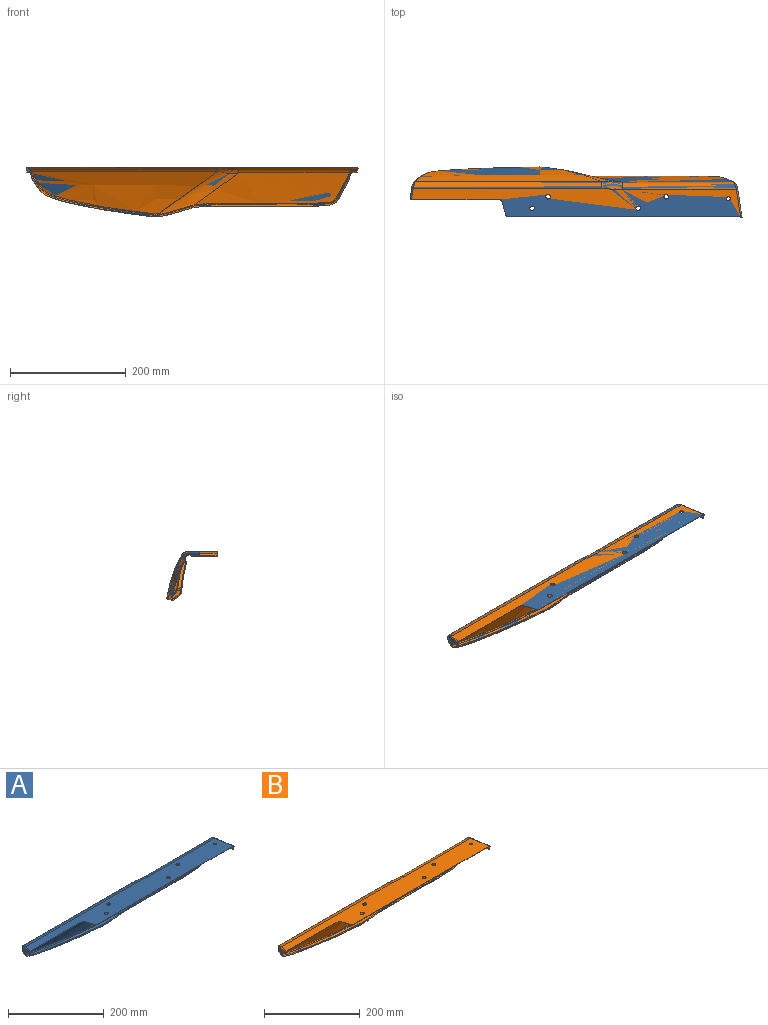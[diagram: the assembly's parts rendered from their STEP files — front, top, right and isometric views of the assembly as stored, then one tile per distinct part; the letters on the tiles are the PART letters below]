
ASSEMBLY  parts=2 mates=1
PART A: 90 faces, bbox 580.2x94.9x176.3 mm
  f0: bspline ~57.87x17.81mm, area 111.5mm2, adj f1,f8,f9,f10
  f1: bspline ~2.59x2.25mm, area 3.8mm2, adj f0,f3,f8,f11
  f2: bspline ~59.87x17.64mm, area 166.5mm2, adj f4,f8,f15,f16,f17
  f3: bspline ~5.04x2.61mm, area 12.2mm2, adj f1,f11,f20,f21
  f4: bspline ~3.74x2.35mm, area 7.8mm2, adj f2,f5,f15,f21
  f5: torus R=36.8mm, axis (0,0.99,0.14), area 2mm2, adj f4,f7,f14,f21
  f6: bspline ~217.18x70.26mm, area 164.9mm2, adj f7,f14,f23,f24
  f7: bspline ~218.59x72.83mm, area 627.5mm2, adj f5,f6,f14,f24,f42
  f8: bspline ~59.27x24.67mm, area 409.1mm2, adj f0,f1,f2,f21,f27
  f9: bspline ~146.09x75.43mm, area 2805mm2, adj f0,f10,f11,f12,f13,f28
  f10: bspline ~2.23x2.04mm, area 2.4mm2, adj f0,f9,f27,f28
  f11: extruded ~321.58x73.69mm, area 17042.7mm2, adj f1,f3,f9,f20,f31
  f12: bspline ~36.97x16.66mm, area 543.4mm2, adj f9,f31,f32,f51
  f13: cylinder r=332.11mm len=267.86mm, axis (-1,0,0), area 5366mm2, adj f9,f29,f32
  f14: cylinder r=36.8mm len=1.03mm, axis (0,0.99,0.14), area 0.7mm2, adj f5,f6,f7,f15,f23,f33
  f15: bspline ~3.73x1.01mm, area 2.1mm2, adj f2,f4,f14,f17,f34,f36
  f16: bspline ~2.22x1.98mm, area 1.2mm2, adj f2,f18,f27,f37
  f17: bspline ~59.5x16.5mm, area 43.8mm2, adj f2,f15,f36,f37
  f18: bspline ~2.25x2mm, area 1.2mm2, adj f16,f27,f38,f39,f40
  f19: bspline ~12.63x8.98mm, area 46.4mm2, adj f20,f31,f41,f42
  f20: bspline ~218.45x77.65mm, area 737.8mm2, adj f3,f11,f19,f42
  f21: cylinder r=35.1mm len=5.62mm, axis (0,-0.99,-0.14), area 22.5mm2, adj f3,f4,f5,f8,f42
  f22: plane 14.14x2.5mm, normal (-0.91,0.14,-0.39), area 9.1mm2, adj f26,f43,f44,f45
  f23: bspline ~218.25x71.79mm, area 370.7mm2, adj f6,f14,f24,f33,f46,f53
  f24: cylinder r=8.22mm len=7.66mm, axis (-0.91,0.14,-0.38), area 5.9mm2, adj f6,f7,f23,f25,f42,f46
  f25: extruded ~7.12x4.52mm, area 6.4mm2, adj f24,f26,f42,f46
  f26: cylinder r=8.22mm len=6.56mm, axis (-0.91,0.14,-0.38), area 5.3mm2, adj f22,f25,f42,f43,f45,f46
  f27: extruded ~5.77x1.11mm, area 5.4mm2, adj f8,f10,f16,f18,f49
  f28: bspline ~6.14x3.79mm, area 13.9mm2, adj f9,f10,f29,f49
  f29: bspline ~273.24x59.78mm, area 873.8mm2, adj f13,f28,f30,f49
  f30: bspline ~13.76x11.39mm, area 56.4mm2, adj f29,f32,f49,f50
  f31: cylinder r=12.8mm len=325.37mm, axis (1,0,0), area 4378.8mm2, adj f11,f12,f19,f51
  f32: cylinder r=12.8mm len=196.45mm, axis (1,0,0), area 3218.4mm2, adj f12,f13,f30,f51
  f33: torus R=36.8mm, axis (0,0.99,0.14), area 1.4mm2, adj f14,f23,f34,f53
  f34: bspline ~3.67x1.43mm, area 4.6mm2, adj f15,f33,f36,f53
  f35: bspline ~219.21x78.81mm, area 1012.1mm2, adj f46,f52,f54,f55
  f36: bspline ~59.48x16.86mm, area 97.9mm2, adj f15,f17,f34,f56,f76
  f37: plane 0.72x0.44mm, normal (0.25,0.14,-0.96), area 0.3mm2, adj f16,f17,f38,f56,f57
  f38: plane 0.7x0.45mm, normal (0.24,0.14,-0.96), area 0.3mm2, adj f18,f37,f40,f57
  f39: bspline ~278.01x57.08mm, area 795.8mm2, adj f18,f40,f49,f59
  f40: bspline ~276.67x54.6mm, area 208.9mm2, adj f18,f38,f39,f57,f59,f60
  f41: cylinder r=1.9mm len=19.81mm, axis (-0.15,-0.99,0), area 72.8mm2, adj f19,f42,f51,f65
  f42: bspline ~226.03x87.31mm, area 1355.3mm2, adj f7,f19,f20,f21,f24,f25,f26,f41
  f43: bspline ~16.19x4.06mm, area 37.4mm2, adj f22,f26,f42,f44,f65
  f44: bspline ~1.29x1.29mm, area 0.4mm2, adj f22,f43,f45,f65
  f45: bspline ~16.16x3.26mm, area 23.4mm2, adj f22,f26,f44,f46,f65
  f46: bspline ~225.86x87.7mm, area 1360.2mm2, adj f23,f24,f25,f26,f35,f45,f52,f53
  f47: bspline ~42.53x6.81mm, area 29.2mm2, adj f48,f61,f62,f68
  f48: bspline ~44.16x8.36mm, area 113.2mm2, adj f47,f49,f62,f68
  f49: bspline ~291.39x79.44mm, area 1902.9mm2, adj f27,f28,f29,f30,f39,f48,f50,f58
  f50: bspline ~48.61x10.3mm, area 179.1mm2, adj f30,f49,f51,f68
  f51: plane 572.5x53.85mm, normal (0,0,-1), area 22246.1mm2, adj f12,f31,f32,f41,f50,f63,f64,f65
  f52: bspline ~13.57x10.12mm, area 65.9mm2, adj f35,f46,f66,f75
  f53: cylinder r=35.8mm len=5.62mm, axis (0,-0.99,-0.14), area 23.1mm2, adj f23,f33,f34,f46,f55,f76
  f54: extruded ~321.58x73.94mm, area 17098.9mm2, adj f35,f55,f75,f77,f88
  f55: bspline ~5.16x3.53mm, area 17mm2, adj f35,f53,f54,f77
  f56: bspline ~1.23x0.99mm, area 0.6mm2, adj f36,f37,f57,f78
  f57: revolved ~101.54x100.52mm, area 498.9mm2, adj f37,f38,f40,f56,f60,f78
  f58: extruded ~7.91x6.39mm, area 8mm2, adj f49,f59,f62,f79
  f59: cylinder r=8.52mm len=7.6mm, axis (0.91,0.14,-0.4), area 6.4mm2, adj f39,f40,f49,f58,f60,f79
  f60: bspline ~277.38x55.93mm, area 469.4mm2, adj f40,f57,f59,f79
  f61: bspline ~44.08x7.55mm, area 67.3mm2, adj f47,f62,f68,f79
  f62: cylinder r=8.52mm len=6.6mm, axis (0.91,0.14,-0.4), area 5.4mm2, adj f47,f48,f49,f58,f61,f79
  f63: plane 22.59x6.05mm, normal (-0.97,-0.26,0), area 16.4mm2, adj f51,f64,f69,f81
  f64: cylinder r=5mm len=4.83mm, axis (0,0,1), area 4.6mm2, adj f51,f63,f65,f81
  f65: plane 154.45x9.53mm, normal (0,-1,0), area 113.4mm2, adj f41,f42,f43,f44,f45,f46,f51,f64
  f66: cylinder r=2.6mm len=20.01mm, axis (-0.15,-0.99,0), area 99.9mm2, adj f46,f52,f65,f81
  f67: bspline ~48.89x11.39mm, area 245.4mm2, adj f68,f79,f80,f81
  f68: plane 403.75x9.65mm, normal (0,-1,0), area 288.1mm2, adj f47,f48,f49,f50,f51,f61,f67,f69
  f69: cylinder r=5mm len=4.83mm, axis (0,0,1), area 4.6mm2, adj f51,f63,f68,f81
  f70: cylinder r=4mm len=8mm, axis (0,0,-1), area 17.6mm2, adj f51,f81
  f71: cylinder r=3.5mm len=7mm, axis (0,0,1), area 15.4mm2, adj f51,f81
  f72: cylinder r=4mm len=8mm, axis (0,0,-1), area 17.6mm2, adj f51,f81
  f73: cylinder r=4mm len=8mm, axis (0,0,-1), area 17.6mm2, adj f51,f81
  f74: cylinder r=4mm len=8mm, axis (0,0,-1), area 17.6mm2, adj f51,f81
  f75: cylinder r=13.5mm len=325.37mm, axis (1,0,0), area 4618.3mm2, adj f52,f54,f81,f82
  f76: bspline ~59.17x24.64mm, area 409.9mm2, adj f36,f53,f77,f78,f83
  f77: bspline ~3.48x3.07mm, area 5.1mm2, adj f54,f55,f76,f83
  f78: extruded ~5.77x1.1mm, area 5.3mm2, adj f56,f57,f76,f79,f84
  f79: bspline ~290.6x78.78mm, area 1907.3mm2, adj f58,f59,f60,f61,f62,f67,f68,f78
  f80: bspline ~14.78x12.52mm, area 79.9mm2, adj f67,f79,f86,f87
  f81: plane 572.79x54.07mm, normal (0,0,1), area 22245.9mm2, adj f63,f64,f65,f66,f67,f68,f69,f70
  f82: bspline ~36.97x17.52mm, area 573mm2, adj f75,f81,f87,f88
  f83: bspline ~58.12x18.63mm, area 153mm2, adj f76,f77,f84,f88
  f84: bspline ~2.96x2.75mm, area 3.2mm2, adj f78,f83,f85,f88
  f85: bspline ~6.2x4.73mm, area 18.8mm2, adj f79,f84,f86,f88
  f86: bspline ~274.1x60.76mm, area 1198.9mm2, adj f79,f80,f85,f89
  f87: cylinder r=13.5mm len=196.45mm, axis (1,0,0), area 3394.4mm2, adj f80,f81,f82,f89
  f88: bspline ~146.12x75.95mm, area 2845mm2, adj f54,f82,f83,f84,f85,f89
  f89: cylinder r=332.81mm len=267.87mm, axis (-1,0,0), area 5377.9mm2, adj f86,f87,f88
PART B: 90 faces, bbox 586.4x101x101.5 mm
  f0: plane 578.95x60.2mm, normal (0,0,1), area 22245.8mm2, adj f1,f3,f4,f5,f6,f7,f8,f9
  f1: cylinder r=4mm len=8mm, axis (0,0,-1), area 20.1mm2, adj f0,f2
  f2: plane 578.79x60.05mm, normal (0,0,-1), area 22245.7mm2, adj f1,f3,f4,f5,f6,f7,f8,f9
  f3: cylinder r=4mm len=8mm, axis (0,0,-1), area 20.1mm2, adj f0,f2
  f4: cylinder r=3.5mm len=7mm, axis (0,0,1), area 17.6mm2, adj f0,f2
  f5: cylinder r=4mm len=8mm, axis (0,0,-1), area 20.1mm2, adj f0,f2
  f6: cylinder r=4mm len=8mm, axis (0,0,-1), area 20.1mm2, adj f0,f2
  f7: plane 22.59x6.05mm, normal (-0.97,-0.26,0), area 18.7mm2, adj f0,f2,f8,f23
  f8: cylinder r=5mm len=4.83mm, axis (0,0,1), area 5.2mm2, adj f0,f2,f7,f9
  f9: plane 403.74x9.73mm, normal (0,-1,0), area 329.2mm2, adj f0,f2,f8,f10,f36,f37,f39,f87
  f10: bspline ~48.89x11.43mm, area 245.4mm2, adj f0,f9,f11,f39
  f11: bspline ~14.78x12.52mm, area 79.9mm2, adj f10,f12,f39,f85
  f12: cylinder r=13.5mm len=196.45mm, axis (1,0,0), area 3394.4mm2, adj f0,f11,f13,f86
  f13: bspline ~36.97x17.52mm, area 573mm2, adj f0,f12,f14,f20
  f14: bspline ~146.12x75.95mm, area 2845.3mm2, adj f13,f15,f17,f83,f84,f86
  f15: bspline ~58.12x18.63mm, area 152.9mm2, adj f14,f16,f47,f83
  f16: bspline ~3.48x3.07mm, area 5.1mm2, adj f15,f17,f47,f82
  f17: extruded ~321.58x73.94mm, area 17116.6mm2, adj f14,f16,f18,f20,f82
  f18: bspline ~219.21x78.81mm, area 1030.6mm2, adj f17,f19,f53,f82
  f19: bspline ~13.57x10.12mm, area 65.9mm2, adj f18,f20,f21,f53
  f20: cylinder r=13.5mm len=325.37mm, axis (1,0,0), area 4618.3mm2, adj f0,f13,f17,f19
  f21: cylinder r=2.6mm len=20.01mm, axis (-0.15,-0.99,0), area 99.9mm2, adj f0,f19,f22,f53
  f22: plane 154.45x9.65mm, normal (0,-1,0), area 129.3mm2, adj f0,f2,f21,f23,f24,f53,f54,f55
  f23: cylinder r=5mm len=4.83mm, axis (0,0,1), area 5.2mm2, adj f0,f2,f7,f22
  f24: cylinder r=1.8mm len=19.78mm, axis (-0.15,-0.99,0), area 68.9mm2, adj f2,f22,f25,f57
  f25: bspline ~12.5x8.82mm, area 43.8mm2, adj f24,f26,f57,f58
  f26: cylinder r=12.7mm len=325.37mm, axis (1,0,0), area 4344.6mm2, adj f2,f25,f27,f59
  f27: bspline ~36.97x16.53mm, area 539.2mm2, adj f2,f26,f28,f34
  f28: bspline ~146.09x75.41mm, area 2797.6mm2, adj f27,f29,f30,f31,f33,f59
  f29: bspline ~57.84x17.69mm, area 105.5mm2, adj f28,f30,f60,f61
  f30: bspline ~2.13x1.94mm, area 2.2mm2, adj f28,f29,f31,f64
  f31: bspline ~6.13x3.66mm, area 13.2mm2, adj f28,f30,f32,f37
  f32: bspline ~273.14x59.64mm, area 826mm2, adj f31,f33,f35,f37
  f33: cylinder r=332.01mm len=267.86mm, axis (-1,0,0), area 11529.5mm2, adj f28,f32,f34
  f34: cylinder r=12.7mm len=196.45mm, axis (1,0,0), area 3193.3mm2, adj f2,f27,f33,f35
  f35: bspline ~13.62x11.23mm, area 53.1mm2, adj f32,f34,f36,f37
  f36: bspline ~48.58x10.17mm, area 169.7mm2, adj f2,f9,f35,f37
  f37: bspline ~291.32x79.38mm, area 1905.2mm2, adj f9,f31,f32,f35,f36,f38,f40,f41
  f38: extruded ~7.92x6.43mm, area 9.1mm2, adj f37,f39,f40,f41
  f39: bspline ~290.6x78.78mm, area 1907.3mm2, adj f9,f10,f11,f38,f40,f41,f42,f44
  f40: cylinder r=8.52mm len=7.72mm, axis (0.91,0.14,-0.4), area 7.4mm2, adj f37,f38,f39,f42,f66,f67
  f41: cylinder r=8.52mm len=6.71mm, axis (0.91,0.14,-0.4), area 6.2mm2, adj f37,f38,f39,f87,f88,f89
  f42: bspline ~277.37x55.92mm, area 468.1mm2, adj f39,f40,f43,f67
  f43: revolved ~1.23x0.87mm, area 0.8mm2, adj f42,f44,f45,f68
  f44: extruded ~5.77x1.1mm, area 5.3mm2, adj f39,f43,f45,f47,f83
  f45: bspline ~1.24x0.99mm, area 0.7mm2, adj f43,f44,f46,f69
  f46: bspline ~59.48x16.86mm, area 98mm2, adj f45,f47,f70,f79
  f47: bspline ~59.17x24.65mm, area 409.8mm2, adj f15,f16,f44,f46,f48
  f48: cylinder r=35.8mm len=5.62mm, axis (0,-0.99,-0.14), area 23.1mm2, adj f47,f49,f50,f53,f79,f82
  f49: torus R=36.8mm, axis (0,0.99,0.14), area 1.4mm2, adj f48,f50,f75,f79
  f50: bspline ~218.25x71.79mm, area 370.2mm2, adj f48,f49,f52,f53,f75,f77
  f51: cylinder r=8.22mm len=6.66mm, axis (-0.91,0.14,-0.38), area 6.2mm2, adj f53,f54,f56,f57,f80,f81
  f52: cylinder r=8.22mm len=7.79mm, axis (-0.91,0.14,-0.38), area 7.2mm2, adj f50,f53,f57,f76,f77,f80
  f53: bspline ~225.86x87.7mm, area 1360.2mm2, adj f18,f19,f21,f22,f48,f50,f51,f52
  f54: bspline ~16.03x3.24mm, area 23.4mm2, adj f22,f51,f53,f55,f81
  f55: bspline ~1.39x1.39mm, area 0.4mm2, adj f22,f54,f56,f81
  f56: bspline ~16.21x4.16mm, area 39.4mm2, adj f22,f51,f55,f57,f81
  f57: bspline ~225.94x87.24mm, area 1354mm2, adj f22,f24,f25,f51,f52,f56,f58,f73
  f58: bspline ~218.34x77.48mm, area 718.5mm2, adj f25,f57,f59,f78
  f59: extruded ~321.58x73.65mm, area 17035.7mm2, adj f26,f28,f58,f60,f78
  f60: bspline ~2.46x2.13mm, area 3.6mm2, adj f29,f59,f61,f78
  f61: bspline ~59.25x24.66mm, area 409mm2, adj f29,f60,f62,f64,f73
  f62: bspline ~59.71x17.87mm, area 176.5mm2, adj f61,f63,f70,f72
  f63: bspline ~2.36x2.12mm, area 1.2mm2, adj f62,f64,f65,f69
  f64: extruded ~5.77x1.11mm, area 5.4mm2, adj f30,f37,f61,f63,f65
  f65: cylinder r=1.8mm len=2.1mm, axis (-0.97,0.02,-0.24), area 1.4mm2, adj f63,f64,f66,f68
  f66: bspline ~277.77x56.48mm, area 842.7mm2, adj f37,f40,f65,f67
  f67: bspline ~276.66x54.61mm, area 238.9mm2, adj f40,f42,f66,f68
  f68: plane 0.87x0.56mm, normal (0.24,0.14,-0.96), area 0.4mm2, adj f43,f65,f67,f69
  f69: plane 0.82x0.44mm, normal (0.25,0.14,-0.96), area 0.3mm2, adj f45,f63,f68,f70
  f70: bspline ~59.53x16.6mm, area 50.1mm2, adj f46,f62,f69,f71
  f71: bspline ~3.74x1.11mm, area 2.4mm2, adj f70,f72,f75,f79
  f72: bspline ~3.72x2.42mm, area 8.3mm2, adj f62,f71,f73,f74
  f73: cylinder r=35mm len=5.62mm, axis (0,-0.99,-0.14), area 22.5mm2, adj f57,f61,f72,f74,f78
  f74: torus R=36.8mm, axis (0,0.99,0.14), area 2.1mm2, adj f72,f73,f75,f76
  f75: cylinder r=36.8mm len=1.03mm, axis (0,0.99,0.14), area 0.8mm2, adj f49,f50,f71,f74,f76,f77
  f76: bspline ~218.27x72.34mm, area 664.4mm2, adj f52,f57,f74,f75,f77
  f77: bspline ~217.18x70.27mm, area 188.1mm2, adj f50,f52,f75,f76
  f78: bspline ~5.02x2.48mm, area 11.5mm2, adj f58,f59,f60,f73
  f79: bspline ~3.82x1.44mm, area 4.6mm2, adj f46,f48,f49,f71
  f80: extruded ~7.14x4.56mm, area 7.3mm2, adj f51,f52,f53,f57
  f81: plane 14.15x2.53mm, normal (-0.91,0.14,-0.39), area 10.4mm2, adj f51,f54,f55,f56
  f82: bspline ~5.18x3.53mm, area 17mm2, adj f16,f17,f18,f48
  f83: bspline ~2.96x2.75mm, area 3.2mm2, adj f14,f15,f44,f84
  f84: bspline ~6.2x4.73mm, area 18.8mm2, adj f14,f39,f83,f85
  f85: bspline ~274.1x60.76mm, area 1198.9mm2, adj f11,f39,f84,f86
  f86: cylinder r=332.81mm len=267.87mm, axis (-1,0,0), area 5377.9mm2, adj f12,f14,f85
  f87: bspline ~44.17x8.45mm, area 119.7mm2, adj f9,f37,f41,f88
  f88: bspline ~42.53x6.85mm, area 33.3mm2, adj f9,f41,f87,f89
  f89: bspline ~44.08x7.55mm, area 67.3mm2, adj f9,f39,f41,f88
PLACE A t=(-280.11,199.61,-0.3)mm
PLACE B t=(-280.11,199.61,-0.3)mm
MATE fastened B.f0 <-> A.f81  axis (0,0,1) through (422.36,295.71,176.86)mm
